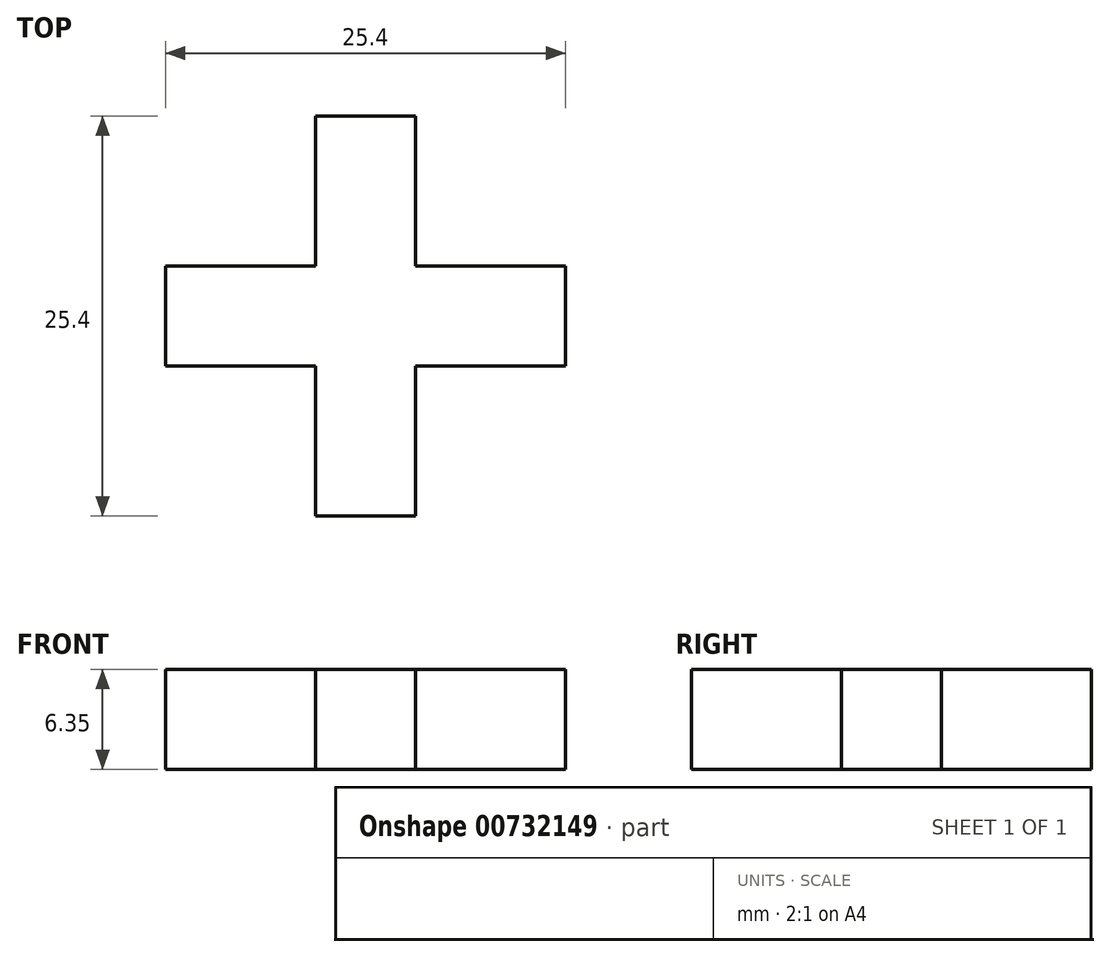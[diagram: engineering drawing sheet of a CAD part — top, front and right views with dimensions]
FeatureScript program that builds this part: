
annotation { "Feature Type Name" : "Feature", "Feature Type Description" : "" }
export const myFeature = defineFeature(function(context is Context, id is Id, definition is map)
    precondition{}
    {
        {
            var Q0;
            Q0=qCreatedBy(makeId("Top.planeOp"),FACE);
            var sketch = newSketch(context, id + "F0", { "sketchPlane" : qUnion([Q0])});
            skLineSegment(sketch, "E0.bottom", {"start": v(3.17, -12.7) * mm, "end": v(-3.18, -12.7) * mm});
            skLineSegment(sketch, "E0.top", {"start": v(3.17, 12.7) * mm, "end": v(-3.18, 12.7) * mm});
            skLineSegment(sketch, "E0.left", {"start": v(12.7, -3.18) * mm, "end": v(12.7, 3.18) * mm});
            skLineSegment(sketch, "E0.right", {"start": v(-12.7, -3.17) * mm, "end": v(-12.7, 3.17) * mm});
            skPoint(sketch, "E0.middle", {"position": v(0, 0) * mm});
            skLineSegment(sketch, "E1.top", {"start": v(-12.7, 3.17) * mm, "end": v(-3.17, 3.18) * mm});
            skLineSegment(sketch, "E1.right", {"start": v(-3.18, 12.7) * mm, "end": v(-3.17, 3.18) * mm});
            skLineSegment(sketch, "E2.top", {"start": v(12.7, 3.18) * mm, "end": v(3.18, 3.18) * mm});
            skLineSegment(sketch, "E2.right", {"start": v(3.17, 12.7) * mm, "end": v(3.18, 3.18) * mm});
            skLineSegment(sketch, "E3.MirrorCS", {"start": v(12.7, -3.18) * mm, "end": v(3.18, -3.18) * mm});
            skLineSegment(sketch, "E4.MirrorCS", {"start": v(3.17, -12.7) * mm, "end": v(3.18, -3.18) * mm});
            skLineSegment(sketch, "E5.MirrorCS", {"start": v(-12.7, -3.17) * mm, "end": v(-3.17, -3.18) * mm});
            skLineSegment(sketch, "E6.MirrorCS", {"start": v(-3.18, -12.7) * mm, "end": v(-3.17, -3.18) * mm});
            skPoint(sketch, "E7.orphan", {"position": v(-12.7, 12.7) * mm});
            skPoint(sketch, "E8.orphan", {"position": v(-12.7, -12.7) * mm});
            skPoint(sketch, "E9.orphan", {"position": v(12.7, -12.7) * mm});
            skPoint(sketch, "E10.orphan", {"position": v(12.7, 12.7) * mm});
            skSolve(sketch);
        }
        {
            var Q0;
            Q0 = qSketchRegion(id + "F0", true);
            extrude(context, id + "F1", {"entities" : qUnion([Q0]), "depth" : 6.35 * mm, "offsetDistance" : 25.4 * mm});
        }
    });
